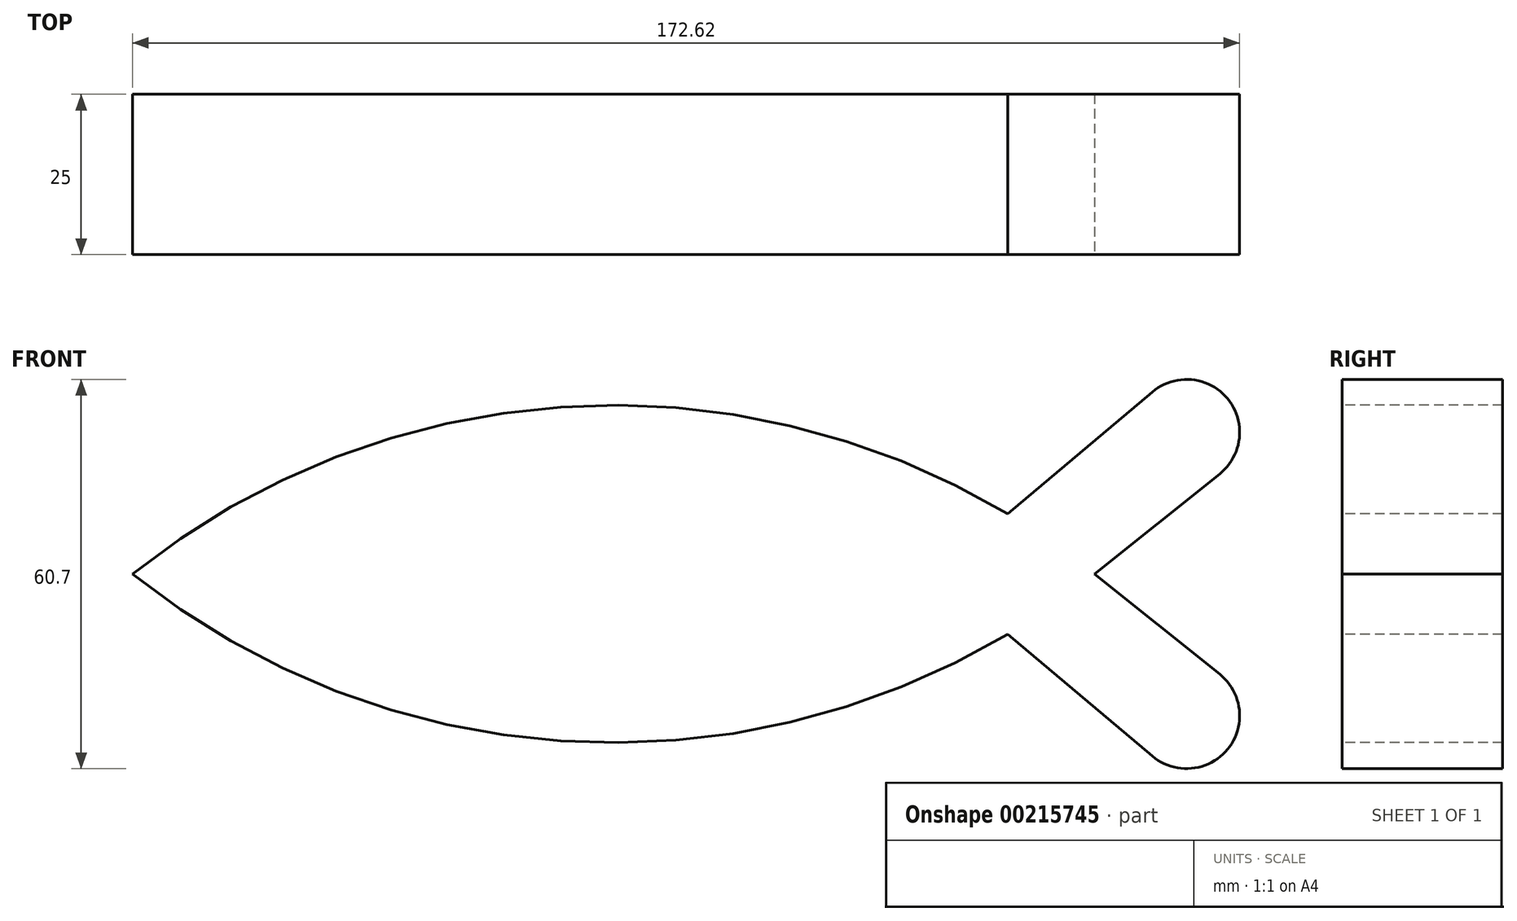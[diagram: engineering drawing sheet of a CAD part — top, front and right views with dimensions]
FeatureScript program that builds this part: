
annotation { "Feature Type Name" : "Feature", "Feature Type Description" : "" }
export const myFeature = defineFeature(function(context is Context, id is Id, definition is map)
    precondition{}
    {
        {
            var Q0;
            Q0=qCreatedBy(makeId("Front.planeOp"),FACE);
            var sketch = newSketch(context, id + "F0", { "sketchPlane" : qUnion([Q0])});
            skArc(sketch, "E0", {"start": v(150, 0) * mm, "mid": v(75, 26.33) * mm, "end": v(0, 0) * mm});
            skArc(sketch, "E1.MirrorCS", {"start": v(150, 0) * mm, "mid": v(75, -26.33) * mm, "end": v(0, 0) * mm});
            skLineSegment(sketch, "E2", {"start": v(0, 0) * mm, "end": v(-19.52, 15.62) * mm});
            skArc(sketch, "E3", {"start": v(-19.52, 15.62) * mm, "mid": v(-20.73, 27.34) * mm, "end": v(-9, 28.4) * mm});
            skLineSegment(sketch, "E4", {"start": v(-9, 28.4) * mm, "end": v(13.52, 9.38) * mm});
            skLineSegment(sketch, "E5.MirrorCS", {"start": v(-9, -28.4) * mm, "end": v(13.52, -9.38) * mm});
            skArc(sketch, "E6.MirrorCS", {"start": v(-19.52, -15.62) * mm, "mid": v(-20.73, -27.34) * mm, "end": v(-9, -28.4) * mm});
            skLineSegment(sketch, "E7.MirrorCS", {"start": v(0, 0) * mm, "end": v(-19.52, -15.62) * mm});
            skSolve(sketch);
        }
        {
            var Q0;
            {var subQ0=sQuery(id+"F0.wireOp",EDGE,"E1.MirrorCS");var subQ1=sQuery(id+"F0.wireOp",EDGE,"E0");var subQ2=makeQuery(id+"F0.imprint","INTERSECT",VERTEX,{"derivedFrom":[subQ1,subQ0]});Q0=makeQuery(id+"F0.imprint","IMPRINT",FACE,{"disambiguationData":[TD([[makeQuery(id+"F0.imprint","IMPRINT",EDGE,{"disambiguationData":[TD([[subQ2,-1.0]])],"derivedFrom":subQ1}),1.0]])]});}
            var Q1;
            {var subQ0=sQuery(id+"F0.wireOp",EDGE,"E2");Q1=makeQuery(id+"F0.imprint","IMPRINT",FACE,{"disambiguationData":[TD([[makeQuery(id+"F0.imprint","IMPRINT",EDGE,{"derivedFrom":subQ0}),-1.0]])]});}
            var Q2;
            {var subQ2=sQuery(id+"F0.wireOp",EDGE,"E5.MirrorCS");Q2=makeQuery(id+"F0.imprint","IMPRINT",FACE,{"disambiguationData":[TD([[makeQuery(id+"F0.imprint","IMPRINT",EDGE,{"derivedFrom":subQ2}),1.0]])]});}
            extrude(context, id + "F1", {"entities" : qUnion([Q0, Q1, Q2]), "oppositeDirection" : true, "depth" : 25 * mm});
        }
        {
            var Q0;
            Q0=makeQuery(id+"F1.opExtrude","SWEPT_BODY",BODY,{"disambiguationData":[OSD([sQuery(id+"F0.wireOp",EDGE,"E0"),sQuery(id+"F0.wireOp",EDGE,"E1.MirrorCS"),sQuery(id+"F0.wireOp",EDGE,"E2"),sQuery(id+"F0.wireOp",EDGE,"E3"),sQuery(id+"F0.wireOp",EDGE,"E4"),sQuery(id+"F0.wireOp",EDGE,"E5.MirrorCS"),sQuery(id+"F0.wireOp",EDGE,"E6.MirrorCS"),sQuery(id+"F0.wireOp",EDGE,"E7.MirrorCS")])]});
            var Q1;
            Q1=makeQuery(id+"F1.opExtrude","SWEPT_EDGE",EDGE,{"disambiguationData":[OSD([sQuery(id+"F0.wireOp",EDGE,"E0"),sQuery(id+"F0.wireOp",EDGE,"E1.MirrorCS")])]});
            var Q2;
            Q2=makeQuery(id+"F1.opExtrude","SWEPT_EDGE",EDGE,{"disambiguationData":[OSD([sQuery(id+"F0.wireOp",EDGE,"E0"),sQuery(id+"F0.wireOp",EDGE,"E1.MirrorCS")])]});
            transform(context, id + "F2", {"entities" : qUnion([Q0]), "transformType" : TransformType.ROTATION, "transformAxis" : qUnion([Q2]), "angle" : 180 * degree, "makeCopy" : false});
        }
    });
